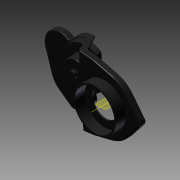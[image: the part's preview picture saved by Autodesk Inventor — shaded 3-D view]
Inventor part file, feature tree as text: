
AUTODESK INVENTOR PART (.ipt)
format: ipt  version: 2011 (Build 150239000, 239)  size: 421,376 bytes
history: native  units: mm (DEFAULTED — no unit token found)
features: sketch x11, extrude x11, fillet x10, other x1, plane x1, shell x1, reference x1
ambient origin geometry x8: Origin, YZ Plane, XZ Plane, XY Plane, X Axis, Y Axis, Z Axis, Center Point
bodies: Solid1 (feature_tree)
feature tree (36):
  sketch  "Sketch1"  dims[d0=0.508mm d1=1.778mm]
  extrude  "Extrusion1"  Depth=1.778mm
  extrude  "Extrusion2"  Depth=2.54mm TaperAngle=0.0deg
  other  "Work Axis1"
  plane  "Work Plane2"
  sketch  "Sketch8"  dims[d2=34.29mm d3=0.0mm d4=2.54mm d5=0.0mm]
  extrude  "Extrusion7"  Depth=2.54mm
  shell  "Shell1"  Thickness=3.175mm
  fillet  "Fillet1"  Radius=1.524mm
  fillet  "Fillet2"  Radius=9.144mm
  extrude  "Extrusion8"  Depth=9.144mm
  extrude  "Extrusion9"  Depth=9.144mm TaperAngle=0.0deg
  fillet  "Fillet5"  Radius=1.524mm
  extrude  "Extrusion10"  Depth=1.524mm
  fillet  "Fillet6"  Radius=1.524mm
  fillet  "Fillet7"  Radius=1.524mm
  fillet  "Fillet8"  Radius=5.08mm
  fillet  "Fillet9"  Radius=0.762mm
  fillet  "Fillet10"  Radius=10.922mm
  extrude  "Extrusion11"  Depth=76.2mm
  fillet  "Fillet11"  Radius=2.54mm
  extrude  "Extrusion12"  Depth=45.72mm
  fillet  "Fillet12"  Radius=17.78mm
  extrude  "Extrusion13"  [1 undecoded]
  extrude  "Extrusion14"  [1 undecoded]
  extrude  "Extrusion15"  [1 undecoded]
  reference  "Reference1"
  sketch  "Sketch9"  dims[d14=2.54mm d15=0.0mm d16=2.54mm d17=3.175mm d18=1.524mm d19=9.144mm d20=-1.047198mm]
  sketch  "Sketch10"  dims[d23=33.02mm d24=9.144mm d25=-1.047198mm]
  sketch  "Sketch12"  dims[d26=1.524mm d27=9.144mm d28=0.0mm d29=1.524mm]
  sketch  "Sketch13"  dims[d30=1.524mm d31=1.524mm d32=1.524mm d33=1.524mm d34=5.08mm d35=0.0mm d36=0.762mm d37=10.922mm d38=0.0mm]
  sketch  "Sketch14"  dims[d39=0.762mm d40=76.2mm d41=2.54mm]
  sketch  "Sketch15"  dims[d42=17.78mm d43=0.0mm d44=45.72mm d45=17.78mm d46=0.0mm]
  sketch  "Sketch16"  dims[d47=12.7mm d48=0.0mm]
  sketch  "Sketch17"
  sketch  "Sketch18"
note: 3 required parameter values undecoded (feature->parameter linkage not recoverable at this tier; creation-order binding heuristic only, values carry confidence <= 0.55)
